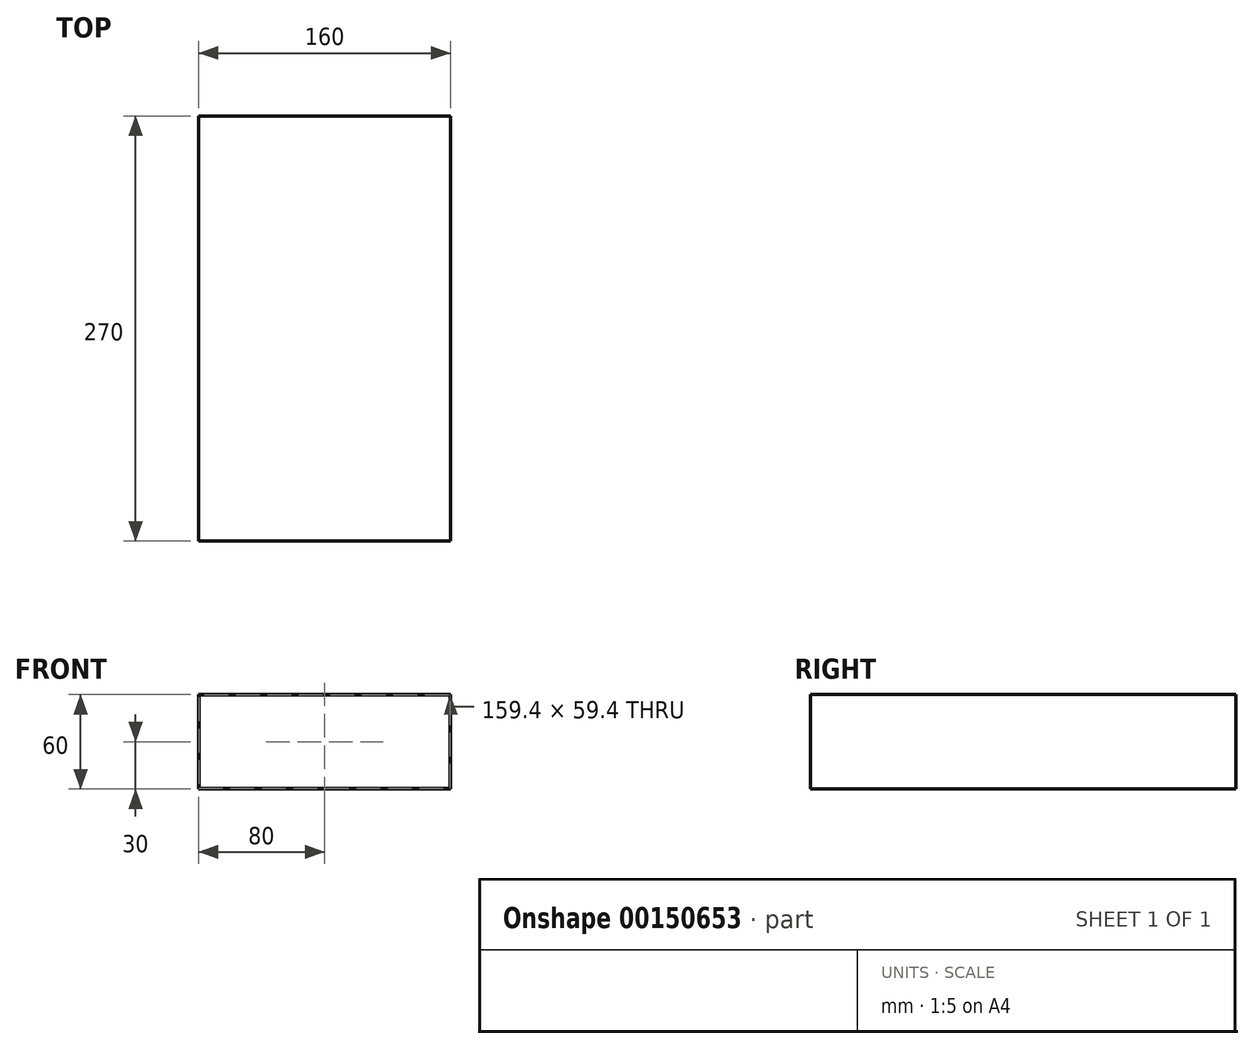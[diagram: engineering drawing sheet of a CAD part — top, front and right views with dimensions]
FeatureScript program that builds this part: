
annotation { "Feature Type Name" : "Feature", "Feature Type Description" : "" }
export const myFeature = defineFeature(function(context is Context, id is Id, definition is map)
    precondition{}
    {
        {
            var Q0;
            Q0=qCreatedBy(makeId("Front.planeOp"),FACE);
            var sketch = newSketch(context, id + "F0", { "sketchPlane" : qUnion([Q0])});
            skLineSegment(sketch, "E0.bottom", {"start": v(80, 30) * mm, "end": v(-80, 30) * mm});
            skLineSegment(sketch, "E0.top", {"start": v(80, -30) * mm, "end": v(-80, -30) * mm});
            skLineSegment(sketch, "E0.left", {"start": v(80, 30) * mm, "end": v(80, -30) * mm});
            skLineSegment(sketch, "E0.right", {"start": v(-80, 30) * mm, "end": v(-80, -30) * mm});
            skPoint(sketch, "E0.middle", {"position": v(0, 0) * mm});
            skLineSegment(sketch, "E1.0", {"start": v(-79.7, 29.7) * mm, "end": v(-79.7, -29.7) * mm});
            skLineSegment(sketch, "E1.1", {"start": v(79.7, 29.7) * mm, "end": v(-79.7, 29.7) * mm});
            skLineSegment(sketch, "E1.2", {"start": v(79.7, 29.7) * mm, "end": v(79.7, -29.7) * mm});
            skLineSegment(sketch, "E1.3", {"start": v(79.7, -29.7) * mm, "end": v(-79.7, -29.7) * mm});
            skSolve(sketch);
        }
        {
            var Q0;
            Q0=makeQuery(id+"F0.imprint","IMPRINT",FACE,{"disambiguationData":[TD([[makeQuery(id+"F0.imprint","IMPRINT",EDGE,{"derivedFrom":sQuery(id+"F0.wireOp",EDGE,"E0.bottom")}),1.0]])]});
            extrude(context, id + "F1", {"entities" : qUnion([Q0]), "endBound" : BoundingType.SYMMETRIC, "depth" : 270 * mm});
        }
    });
